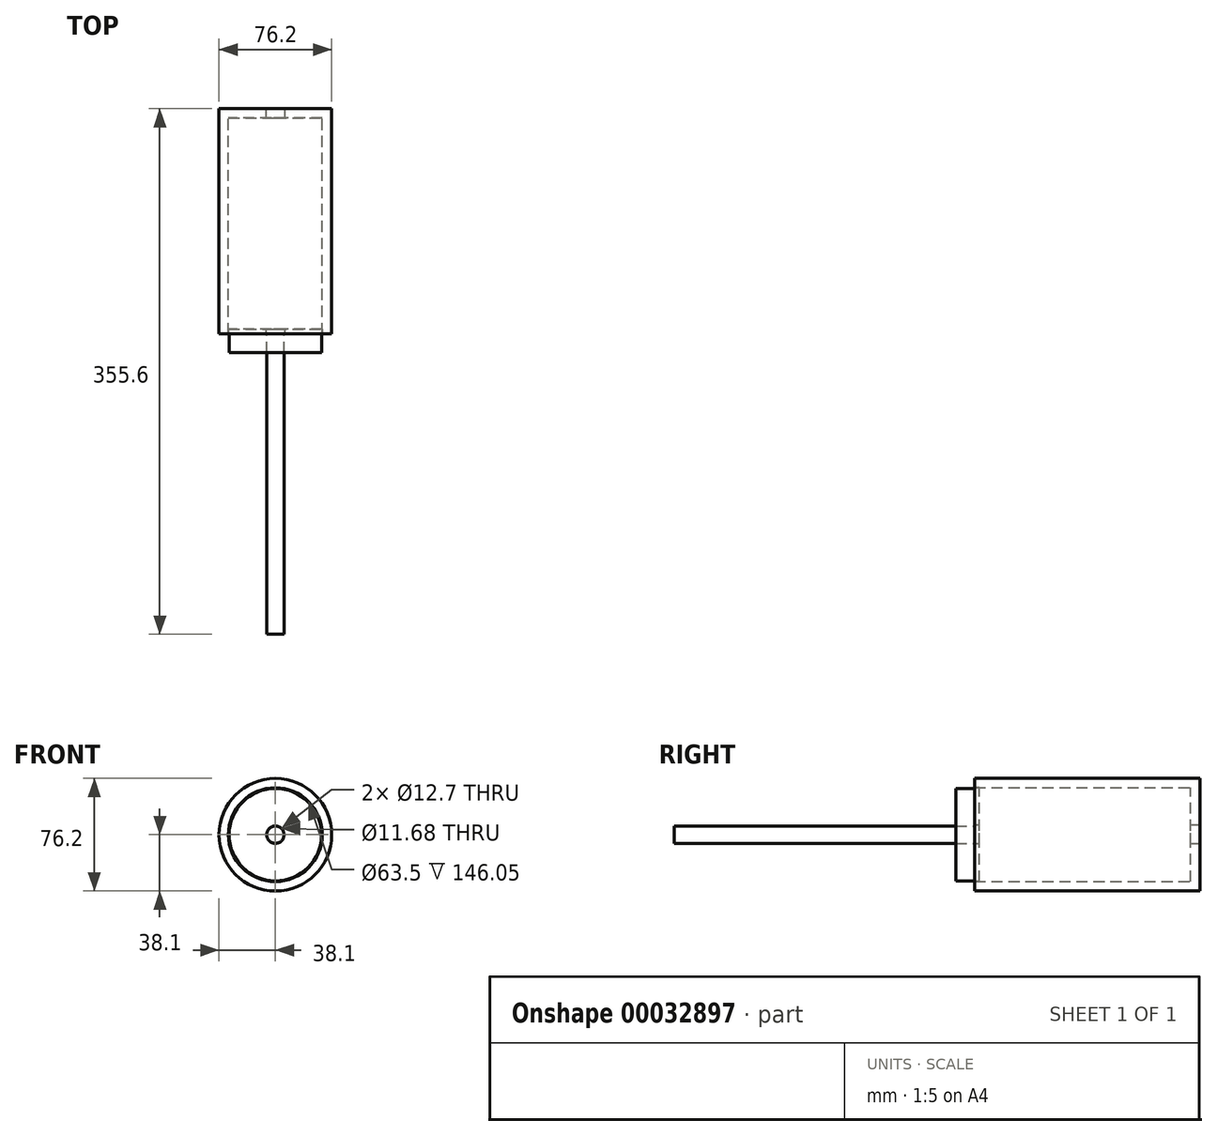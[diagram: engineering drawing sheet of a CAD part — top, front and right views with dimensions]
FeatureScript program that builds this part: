
annotation { "Feature Type Name" : "Feature", "Feature Type Description" : "" }
export const myFeature = defineFeature(function(context is Context, id is Id, definition is map)
    precondition{}
    {
        {
            var Q0;
            Q0=qCreatedBy(makeId("Front.planeOp"),FACE);
            var sketch = newSketch(context, id + "F0", { "sketchPlane" : qUnion([Q0])});
            skCircle(sketch, "E0", {"center": v(0, 0) * mm, "radius": 38.1 * mm});
            skSolve(sketch);
        }
        {
            var Q0;
            Q0=makeQuery(id+"F0.imprint","IMPRINT",FACE,{"disambiguationData":[TD([[makeQuery(id+"F0.imprint","IMPRINT",EDGE,{"derivedFrom":sQuery(id+"F0.wireOp",EDGE,"E0")}),1.0]])]});
            extrude(context, id + "F1", {"entities" : qUnion([Q0]), "endBound" : BoundingType.SYMMETRIC, "depth" : 152.4 * mm});
        }
        {
            var Q0;
            Q0=makeQuery(id+"F1.opExtrude","CAP_FACE",FACE,{"disambiguationData":[OSD([sQuery(id+"F0.wireOp",EDGE,"E0")])],"isStart":false});
            shell(context, id + "F2", {"entities" : qUnion([Q0]), "thickness" : 6.35 * mm});
        }
        {
            var Q0;
            Q0=makeQuery(id+"F1.opExtrude","CAP_FACE",FACE,{"disambiguationData":[OSD([sQuery(id+"F0.wireOp",EDGE,"E0")])],"isStart":false});
            var sketch = newSketch(context, id + "F3", { "sketchPlane" : qUnion([Q0])});
            skCircle(sketch, "E1", {"center": v(0, 0) * mm, "radius": 31.75 * mm});
            skSolve(sketch);
        }
        {
            var Q0;
            Q0 = qSketchRegion(id + "F3", true);
            extrude(context, id + "F4", {"entities" : qUnion([Q0]), "oppositeDirection" : true, "depth" : 3.17 * mm});
        }
        {
            var Q0;
            Q0=makeQuery(id+"F4.opExtrude","CAP_FACE",FACE,{"disambiguationData":[OSD([sQuery(id+"F3.wireOp",EDGE,"E1")])],"isStart":true});
            var sketch = newSketch(context, id + "F5", { "sketchPlane" : qUnion([Q0])});
            skCircle(sketch, "E2.0.0", {"center": v(0, 0) * mm, "radius": 31.75 * mm});
            skCircle(sketch, "E3", {"center": v(0, 0) * mm, "radius": 6.35 * mm});
            skSolve(sketch);
        }
        {
            var Q0;
            Q0=makeQuery(id+"F5.imprint","IMPRINT",FACE,{"disambiguationData":[TD([[makeQuery(id+"F5.imprint","IMPRINT",EDGE,{"derivedFrom":sQuery(id+"F5.wireOp",EDGE,"E3")}),1.0]])]});
            extrude(context, id + "F6", {"entities" : qUnion([Q0]), "operationType" : NewBodyOperationType.REMOVE, "endBound" : BoundingType.THROUGH_ALL, "oppositeDirection" : true, "depth" : 25.4 * mm});
        }
        {
            var Q0;
            Q0=makeQuery(id+"F4.opExtrude","CAP_FACE",FACE,{"disambiguationData":[OSD([sQuery(id+"F3.wireOp",EDGE,"E1")])],"isStart":true});
            var sketch = newSketch(context, id + "F7", { "sketchPlane" : qUnion([Q0])});
            skCircle(sketch, "E4.0", {"center": v(0, 0) * mm, "radius": 6.35 * mm});
            skCircle(sketch, "E5", {"center": v(0, 0) * mm, "radius": 5.84 * mm});
            skSolve(sketch);
        }
        {
            var Q0;
            Q0=makeQuery(id+"F7.imprint","IMPRINT",FACE,{"disambiguationData":[TD([[makeQuery(id+"F7.imprint","IMPRINT",EDGE,{"derivedFrom":sQuery(id+"F7.wireOp",EDGE,"E5")}),1.0]])]});
            extrude(context, id + "F8", {"entities" : qUnion([Q0]), "depth" : 203.2 * mm});
        }
        {
            var Q0;
            Q0=makeQuery(id+"F8.opExtrude","CAP_FACE",FACE,{"disambiguationData":[OSD([sQuery(id+"F7.wireOp",EDGE,"E5")])],"isStart":true});
            var sketch = newSketch(context, id + "F9", { "sketchPlane" : qUnion([Q0])});
            skCircle(sketch, "E6", {"center": v(0, 0) * mm, "radius": 31.24 * mm});
            skCircle(sketch, "E7.0", {"center": v(0, 0) * mm, "radius": 31.75 * mm});
            skSolve(sketch);
        }
        {
            var Q0;
            Q0=makeQuery(id+"F9.imprint","IMPRINT",FACE,{"disambiguationData":[TD([[makeQuery(id+"F9.imprint","IMPRINT",EDGE,{"derivedFrom":sQuery(id+"F9.wireOp",EDGE,"E6")}),1.0]])]});
            extrude(context, id + "F10", {"entities" : qUnion([Q0]), "oppositeDirection" : true, "depth" : 12.7 * mm});
        }
    });
